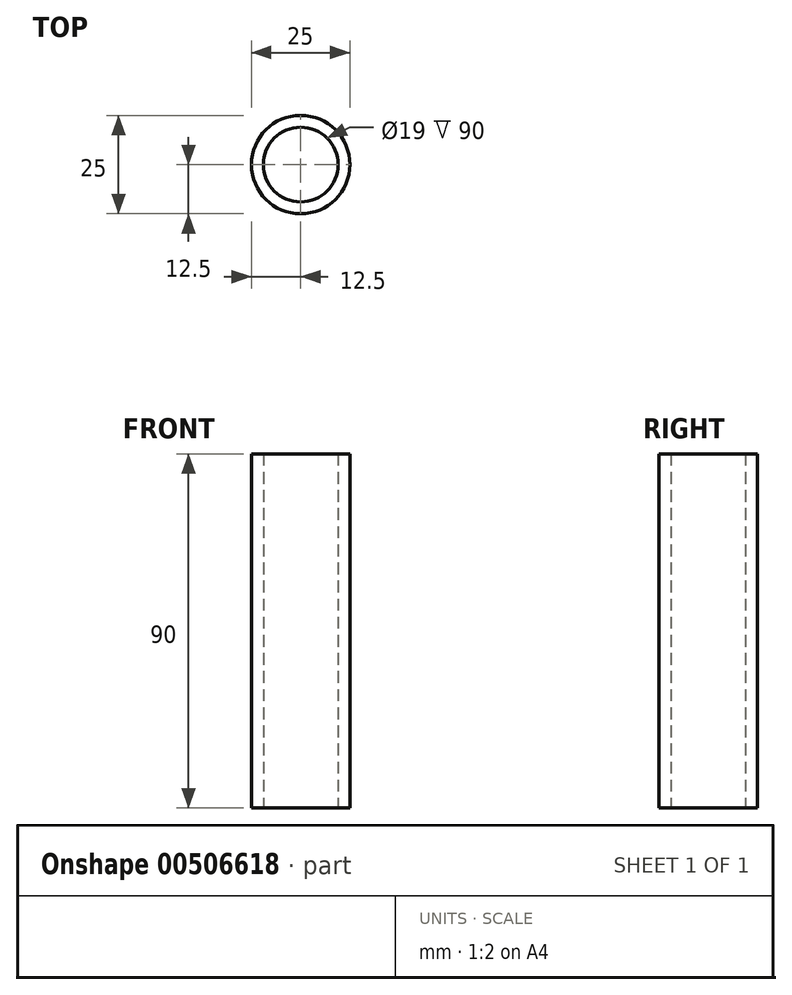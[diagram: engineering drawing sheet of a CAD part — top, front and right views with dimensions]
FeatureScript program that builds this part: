
annotation { "Feature Type Name" : "Feature", "Feature Type Description" : "" }
export const myFeature = defineFeature(function(context is Context, id is Id, definition is map)
    precondition{}
    {
        {
            var Q0;
            Q0=qCreatedBy(makeId("Top.planeOp"),FACE);
            var sketch = newSketch(context, id + "F0", { "sketchPlane" : qUnion([Q0])});
            skCircle(sketch, "E0", {"center": v(0, 0) * mm, "radius": 12.5 * mm});
            skCircle(sketch, "E1", {"center": v(0, 0) * mm, "radius": 9.5 * mm});
            skSolve(sketch);
        }
        {
            var Q0;
            Q0 = qSketchRegion(id + "F0", true);
            extrude(context, id + "F1", {"entities" : qUnion([Q0]), "depth" : 90 * mm});
        }
    });
